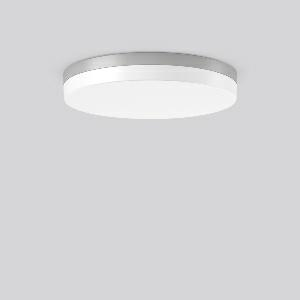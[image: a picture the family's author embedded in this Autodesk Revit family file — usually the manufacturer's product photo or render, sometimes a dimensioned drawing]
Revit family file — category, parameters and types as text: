
# Revit family: flat_slim_round_312634_004_19_adc9
name_source: partatom
category: Lighting Fixtures
units: mm (PartAtom-declared; Revit-internal decimal feet)

## family parameters
Cut with Voids When Loaded = No
Host = Face
Light Source = No
Part Type = Normal
Room Calculation Point = No
Round Connector Dimension = Use Diameter
Shared = No

## types (1)
- MultiLumen 1 830 (1 x LED Modul 830, 3450 lm, 3000)
    Apparent Load = 26 VA
    CIE Flux Codes = 40 71 90 84 100
    Color Rendering = 80
    Color Temperature = 3000
    Default Elevation = 1800 mm
    Height = 70 mm
    Lamp = 1 x LED Modul 830
    Lamp Light Flux = 3450 lm
    Lamp count = 1
    Length = 480 mm
    Lifetime = 50000 h
    Luminous efficacy = 133 lm/W
    Manufacturer = RZB
    ModVariant = No
    Model = 312634.004.19
    Mounting Place = Ceiling
    Mounting Type = Surface mounted
    Number of Poles = 1
    OnlyDefault = Yes
    Power Factor = 1
    Product Name = FLAT SLIM round
    Product group = Surface mounted ceiling and wall luminaires
    ProductGroupID = 305
    Protection Class = Protection class I
    Protection Degree = Degree of protection
    RLX_Detail_Level = 1
    RLX_Emergency_Light_Flux = 0 lm
    RLX_Emergency_Type = 0
    RLX_Emergency_Type_DB = No
    RlxData = <blob elided: 22353 chars, md5=299373d8>
    Socket = socket
    Standby Power = 0 W
    System Light Flux = 3450 lm
    System Power = 26 W
    Type Comments = MultiLumen 1 830
    Type Image = 312633.004.jpg
    URL = http://relux.com
    VarID = multilumen_1_830
    Voltage = 0 V
    Weight = 0.00 kg
    Width = 0 mm  [stored 0 ft]

note: [stored X ft] marks values corroborated as IEEE doubles in the binary element streams (Revit-internal decimal feet)

## geometry (parser evidence)
native form markers: Blend x4, Sweep x13
no freeform markers — native parametric forms only
